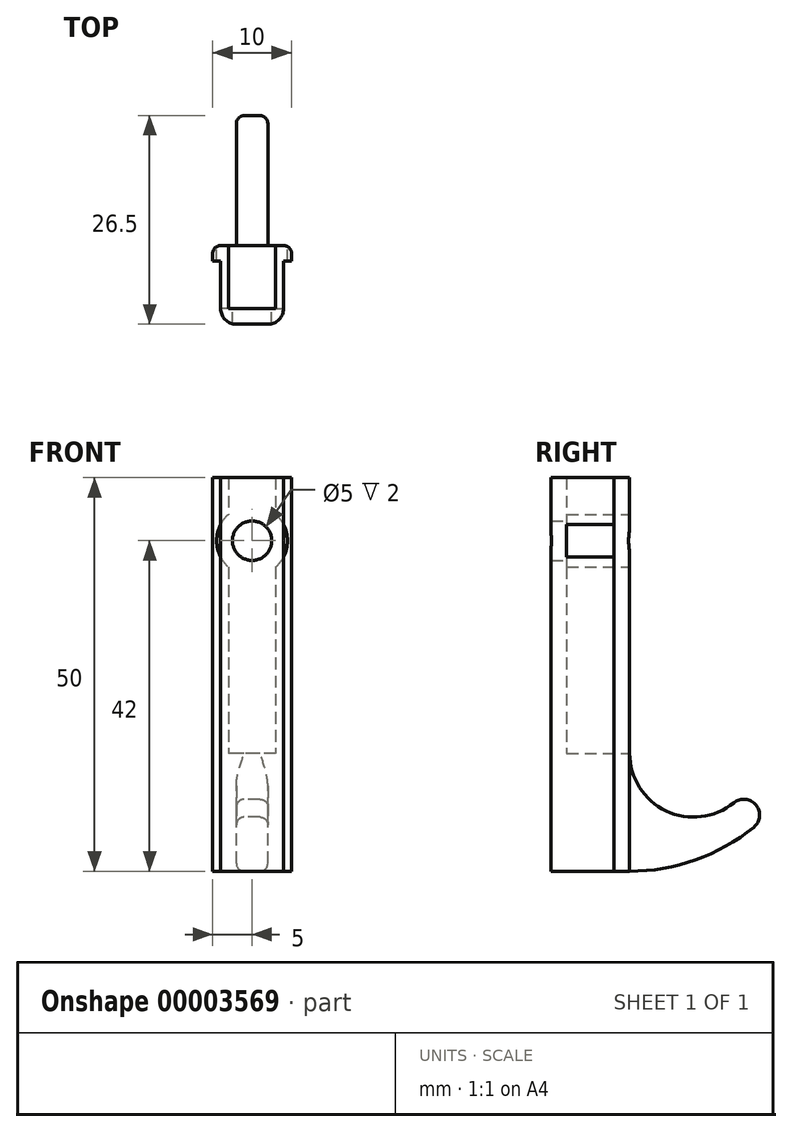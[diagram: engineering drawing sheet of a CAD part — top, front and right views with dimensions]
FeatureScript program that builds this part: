
annotation { "Feature Type Name" : "Feature", "Feature Type Description" : "" }
export const myFeature = defineFeature(function(context is Context, id is Id, definition is map)
    precondition{}
    {
        {
            var Q0;
            Q0=qCreatedBy(makeId("Top.planeOp"),FACE);
            var sketch = newSketch(context, id + "F0", { "sketchPlane" : qUnion([Q0])});
            skLineSegment(sketch, "E0", {"start": v(-5, 0) * mm, "end": v(5, 0) * mm});
            skLineSegment(sketch, "E1", {"start": v(5, 0) * mm, "end": v(5, -2) * mm});
            skLineSegment(sketch, "E2", {"start": v(5, -2) * mm, "end": v(4, -2) * mm});
            skLineSegment(sketch, "E3", {"start": v(4, -2) * mm, "end": v(4, -10) * mm});
            skLineSegment(sketch, "E4", {"start": v(4, -10) * mm, "end": v(-4, -10) * mm});
            skLineSegment(sketch, "E5", {"start": v(-4, -10) * mm, "end": v(-4, -2) * mm});
            skLineSegment(sketch, "E6", {"start": v(-4, -2) * mm, "end": v(-5, -2) * mm});
            skLineSegment(sketch, "E7", {"start": v(-5, -2) * mm, "end": v(-5, 0) * mm});
            skSolve(sketch);
        }
        {
            var Q0;
            Q0=makeQuery(id+"F0.imprint","IMPRINT",FACE,{"disambiguationData":[TD([[makeQuery(id+"F0.imprint","IMPRINT",EDGE,{"derivedFrom":sQuery(id+"F0.wireOp",EDGE,"E0")}),-1.0]])]});
            extrude(context, id + "F1", {"entities" : qUnion([Q0]), "depth" : 50 * mm});
        }
        {
            var Q0;
            Q0=makeQuery(id+"F1.opExtrude","SWEPT_FACE",FACE,{"disambiguationData":[OSD([sQuery(id+"F0.wireOp",EDGE,"E0")])]});
            var sketch = newSketch(context, id + "F2", { "sketchPlane" : qUnion([Q0])});
            skLineSegment(sketch, "E8.bottom", {"start": v(-3, 50) * mm, "end": v(3, 50) * mm});
            skLineSegment(sketch, "E8.top", {"start": v(-3, 15) * mm, "end": v(3, 15) * mm});
            skLineSegment(sketch, "E8.left", {"start": v(-3, 50) * mm, "end": v(-3, 15) * mm});
            skLineSegment(sketch, "E8.right", {"start": v(3, 50) * mm, "end": v(3, 15) * mm});
            skLineSegment(sketch, "E9", {"start": v(0, 0) * mm, "end": v(0, 15) * mm, "construction": true});
            skSolve(sketch);
        }
        {
            var Q0;
            Q0 = qSketchRegion(id + "F2", true);
            extrude(context, id + "F3", {"entities" : qUnion([Q0]), "operationType" : NewBodyOperationType.REMOVE, "oppositeDirection" : true, "depth" : 8 * mm});
        }
        {
            var Q0;
            Q0=makeQuery(id+"F1.opExtrude","SWEPT_FACE",FACE,{"disambiguationData":[OSD([sQuery(id+"F0.wireOp",EDGE,"E0")])]});
            var sketch = newSketch(context, id + "F4", { "sketchPlane" : qUnion([Q0])});
            skCircle(sketch, "E10", {"center": v(0, 42) * mm, "radius": 4.5 * mm});
            skSolve(sketch);
        }
        {
            var Q0;
            Q0 = qSketchRegion(id + "F4", true);
            var Q1;
            Q1=makeQuery(id+"F3.boolean.opBoolean","COPY",FACE,{"derivedFrom":makeQuery(id+"F3.opExtrude","CAP_FACE",FACE,{"disambiguationData":[OSD([sQuery(id+"F2.wireOp",EDGE,"E8.bottom"),sQuery(id+"F2.wireOp",EDGE,"E8.top"),sQuery(id+"F2.wireOp",EDGE,"E8.left"),sQuery(id+"F2.wireOp",EDGE,"E8.right")])],"isStart":false})});
            extrude(context, id + "F5", {"entities" : qUnion([Q0]), "operationType" : NewBodyOperationType.REMOVE, "endBound" : BoundingType.UP_TO_SURFACE, "oppositeDirection" : true, "endBoundEntityFace" : qUnion([Q1]), "depth" : 8 * mm});
        }
        {
            var Q0;
            Q0=makeQuery(id+"F5.boolean.opBoolean","MERGE",FACE,{"derivedFrom":[makeQuery(id+"F3.boolean.opBoolean","COPY",FACE,{"derivedFrom":makeQuery(id+"F3.opExtrude","CAP_FACE",FACE,{"disambiguationData":[OSD([sQuery(id+"F2.wireOp",EDGE,"E8.bottom"),sQuery(id+"F2.wireOp",EDGE,"E8.top"),sQuery(id+"F2.wireOp",EDGE,"E8.left"),sQuery(id+"F2.wireOp",EDGE,"E8.right")])],"isStart":false})}),makeQuery(id+"F5.opExtrude","CAP_FACE",FACE,{"disambiguationData":[OSD([sQuery(id+"F4.wireOp",EDGE,"E10")])],"isStart":false})]});
            var sketch = newSketch(context, id + "F6", { "sketchPlane" : qUnion([Q0])});
            skCircle(sketch, "E11", {"center": v(0, 42) * mm, "radius": 2.5 * mm});
            skSolve(sketch);
        }
        {
            var Q0;
            Q0 = qSketchRegion(id + "F6", true);
            extrude(context, id + "F7", {"entities" : qUnion([Q0]), "operationType" : NewBodyOperationType.REMOVE, "oppositeDirection" : true, "depth" : 25 * mm});
        }
        {
            var Q0;
            Q0=makeQuery(id+"F1.opExtrude","SWEPT_EDGE",EDGE,{"disambiguationData":[OSD([sQuery(id+"F0.wireOp",EDGE,"E3"),sQuery(id+"F0.wireOp",EDGE,"E4")])]});
            var Q1;
            Q1=makeQuery(id+"F1.opExtrude","SWEPT_EDGE",EDGE,{"disambiguationData":[OSD([sQuery(id+"F0.wireOp",EDGE,"E4"),sQuery(id+"F0.wireOp",EDGE,"E5")])]});
            fillet(context, id + "F8", {"entities" : qUnion([Q0, Q1]), "radius" : 2 * mm, "tangentPropagation" : true, "allowEdgeOverflow" : false});
        }
        {
            var Q0;
            Q0=qCreatedBy(makeId("Right.planeOp"),FACE);
            var sketch = newSketch(context, id + "F9", { "sketchPlane" : qUnion([Q0])});
            skLineSegment(sketch, "E12", {"start": v(0, 0) * mm, "end": v(0, 15) * mm});
            skArc(sketch, "E13", {"start": v(0, 15) * mm, "mid": v(4.63, 7.67) * mm, "end": v(13.24, 8.7) * mm});
            skArc(sketch, "E14", {"start": v(15.76, 5.6) * mm, "mid": v(16.05, 8.42) * mm, "end": v(13.24, 8.7) * mm});
            skArc(sketch, "E15", {"start": v(0, 0) * mm, "mid": v(8.36, 1.44) * mm, "end": v(15.76, 5.6) * mm});
            skLineSegment(sketch, "E16", {"start": v(13.24, 8.7) * mm, "end": v(15.76, 5.6) * mm, "construction": true});
            skSolve(sketch);
        }
        {
            var Q0;
            Q0 = qSketchRegion(id + "F9", true);
            extrude(context, id + "F10", {"entities" : qUnion([Q0]), "operationType" : NewBodyOperationType.ADD, "depth" : 2 * mm});
        }
        {
            var Q0;
            Q0=makeQuery(id+"F10.opExtrude","CAP_FACE",FACE,{"disambiguationData":[OSD([sQuery(id+"F9.wireOp",EDGE,"E12"),sQuery(id+"F9.wireOp",EDGE,"E13"),sQuery(id+"F9.wireOp",EDGE,"E14"),sQuery(id+"F9.wireOp",EDGE,"E15")])],"isStart":true});
            extrude(context, id + "F11", {"entities" : qUnion([Q0]), "operationType" : NewBodyOperationType.ADD, "depth" : 2 * mm});
        }
        {
            var Q0;
            Q0=makeQuery(id+"F10.opExtrude","CAP_EDGE",EDGE,{"disambiguationData":[OSD([sQuery(id+"F9.wireOp",EDGE,"E13")])],"isStart":false});
            var Q1;
            Q1=makeQuery(id+"F11.opExtrude","CAP_EDGE",EDGE,{"disambiguationData":[OSD([sQuery(id+"F9.wireOp",EDGE,"E13")])],"isStart":false});
            fillet(context, id + "F12", {"entities" : qUnion([Q0, Q1]), "radius" : 1 * mm, "tangentPropagation" : true, "allowEdgeOverflow" : false});
        }
        {
            var Q0;
            Q0=makeQuery(id+"F1.opExtrude","SWEPT_EDGE",EDGE,{"disambiguationData":[OSD([sQuery(id+"F0.wireOp",EDGE,"E0"),sQuery(id+"F0.wireOp",EDGE,"E1")])]});
            var Q1;
            Q1=makeQuery(id+"F1.opExtrude","SWEPT_EDGE",EDGE,{"disambiguationData":[OSD([sQuery(id+"F0.wireOp",EDGE,"E0"),sQuery(id+"F0.wireOp",EDGE,"E7")])]});
            fillet(context, id + "F13", {"entities" : qUnion([Q0, Q1]), "radius" : 1 * mm, "tangentPropagation" : true, "allowEdgeOverflow" : false});
        }
    });
